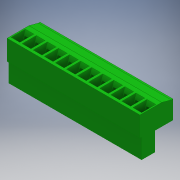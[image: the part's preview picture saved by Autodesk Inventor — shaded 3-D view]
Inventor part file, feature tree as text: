
AUTODESK INVENTOR PART (.ipt)
format: ipt  version: 2018 (Build 220112000, 112)  size: 349,696 bytes
history: native  units: mm
features: extrude x5, sketch x5, chamfer x4, projected_geometry x3, plane x2, mirror x1, pattern_linear x1
ambient origin geometry x8: Origin, YZ Plane, XZ Plane, XY Plane, X Axis, Y Axis, Z Axis, Center Point
bodies: Solid1 (feature_tree)
feature tree (21):
  extrude  "Extrusion1"  Depth=18.2mm
  extrude  "Extrusion2"  TaperAngle=165.0deg  [1 undecoded]
  extrude  "Extrusion3"  Depth=6.0mm
  chamfer  "Chamfer1"  Distance=35.0mm
  chamfer  "Chamfer2"  Distance=10.0mm
  chamfer  "Chamfer3"  Distance=60.96mm
  chamfer  "Chamfer4"  Distance=2.54mm
  extrude  "Extrusion4"  Depth=3.0mm
  plane  "Work Plane1"
  extrude  "Extrusion5"  Depth=4.0mm
  plane  "Work Plane2"
  mirror  "Mirror1"
  pattern_linear  "Rectangular Pattern1"  Spacing1=3.8mm  [1 undecoded]
  sketch  "Sketch1"  dims[d3=8.6mm d4=18.2mm]
  sketch  "Sketch2"  dims[d5=15.1mm d6=165.0deg]
  projected_geometry  "Projected Loop1"
  sketch  "Sketch3"  dims[d7=0.75mm d8=6.0mm]
  sketch  "Sketch4"  dims[d9=9.2mm]
  projected_geometry  "Projected Loop2"
  sketch  "Sketch6"  dims[d10=0.75mm d11=35.0mm d12=10.0mm d13=60.96mm d14=0.0mm d15=2.54mm d16=3.0mm d17=4.0mm d25=3.8mm d26=10.0mm d27=0.0mm d28=1.8mm d29=10.0mm d30=0.0mm d31=2.0mm d32=4.0mm d33=45.0deg d34=0.5mm d35=4.0mm d36=45.0deg d37=0.5mm d38=4.0mm d39=45.0deg d40=0.5mm d41=4.0mm d42=45.0deg d43=120.0mm d45=5.08mm d46=5.5mm d47=2.54mm d48=2.5mm d49=1.27mm d50=2.54mm d51=3.5mm d52=10.0mm d53=0.0mm d54=-10.16mm d55=2.54mm d56=0.0mm]
  projected_geometry  "Projected Loop3"
note: 2 required parameter values undecoded (feature->parameter linkage not recoverable at this tier; creation-order binding heuristic only, values carry confidence <= 0.55)
